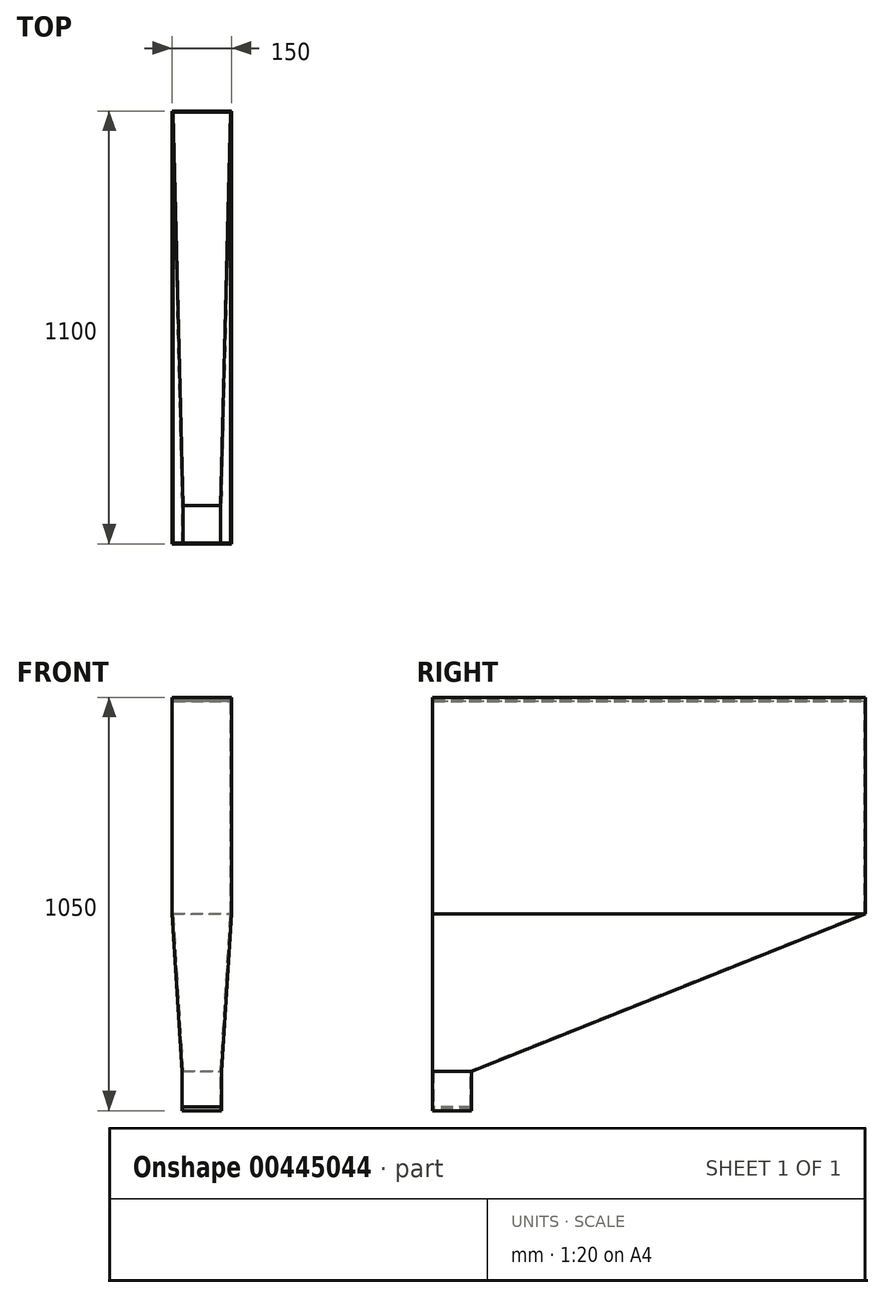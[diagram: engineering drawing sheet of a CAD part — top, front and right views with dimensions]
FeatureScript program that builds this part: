
annotation { "Feature Type Name" : "Feature", "Feature Type Description" : "" }
export const myFeature = defineFeature(function(context is Context, id is Id, definition is map)
    precondition{}
    {
        {
            var Q0;
            Q0=qCreatedBy(makeId("Front.planeOp"),FACE);
            var sketch = newSketch(context, id + "F0", { "sketchPlane" : qUnion([Q0])});
            skLineSegment(sketch, "E0.bottom", {"start": v(-75, 0) * mm, "end": v(75, 0) * mm});
            skLineSegment(sketch, "E0.top", {"start": v(-75, 550) * mm, "end": v(75, 550) * mm});
            skLineSegment(sketch, "E0.left", {"start": v(-75, 0) * mm, "end": v(-75, 550) * mm});
            skLineSegment(sketch, "E0.right", {"start": v(75, 0) * mm, "end": v(75, 550) * mm});
            skLineSegment(sketch, "E1.bottom", {"start": v(-50, -400) * mm, "end": v(50, -400) * mm});
            skLineSegment(sketch, "E1.top", {"start": v(-50, -500) * mm, "end": v(50, -500) * mm});
            skLineSegment(sketch, "E1.left", {"start": v(-50, -400) * mm, "end": v(-50, -500) * mm});
            skLineSegment(sketch, "E1.right", {"start": v(50, -400) * mm, "end": v(50, -500) * mm});
            skLineSegment(sketch, "E2", {"start": v(-75, 0) * mm, "end": v(-50, -400) * mm});
            skLineSegment(sketch, "E3", {"start": v(50, -400) * mm, "end": v(75, 0) * mm});
            skSolve(sketch);
        }
        {
            var Q0;
            Q0=makeQuery(id+"F0.imprint","IMPRINT",FACE,{"disambiguationData":[TD([[makeQuery(id+"F0.imprint","IMPRINT",EDGE,{"derivedFrom":sQuery(id+"F0.wireOp",EDGE,"E1.bottom")}),-1.0]])]});
            var Q1;
            Q1=makeQuery(id+"F0.imprint","IMPRINT",FACE,{"disambiguationData":[TD([[makeQuery(id+"F0.imprint","IMPRINT",EDGE,{"derivedFrom":sQuery(id+"F0.wireOp",EDGE,"E0.bottom")}),1.0]])]});
            var Q2;
            Q2=makeQuery(id+"F0.imprint","IMPRINT",FACE,{"disambiguationData":[TD([[makeQuery(id+"F0.imprint","IMPRINT",EDGE,{"derivedFrom":sQuery(id+"F0.wireOp",EDGE,"E0.bottom")}),-1.0]])]});
            extrude(context, id + "F1", {"entities" : qUnion([Q0, Q1, Q2]), "endBound" : BoundingType.SYMMETRIC, "depth" : 1100 * mm});
        }
        {
            var Q0;
            Q0=makeQuery(id+"F1.opExtrude","SWEPT_FACE",FACE,{"disambiguationData":[OSD([sQuery(id+"F0.wireOp",EDGE,"E0.right")])]});
            var sketch = newSketch(context, id + "F2", { "sketchPlane" : qUnion([Q0])});
            skLineSegment(sketch, "E4", {"start": v(550, 0) * mm, "end": v(550, -500) * mm});
            skLineSegment(sketch, "E5", {"start": v(550, -500) * mm, "end": v(-450, -500) * mm});
            skLineSegment(sketch, "E6", {"start": v(-450, -500) * mm, "end": v(-450, -400) * mm});
            skLineSegment(sketch, "E7", {"start": v(-450, -400) * mm, "end": v(550, 0) * mm});
            skSolve(sketch);
        }
        {
            var Q0;
            Q0=makeQuery(id+"F2.imprint","IMPRINT",FACE,{"disambiguationData":[TD([[makeQuery(id+"F2.imprint","IMPRINT",EDGE,{"derivedFrom":sQuery(id+"F2.wireOp",EDGE,"E4")}),-1.0]])]});
            extrude(context, id + "F3", {"entities" : qUnion([Q0]), "operationType" : NewBodyOperationType.REMOVE, "oppositeDirection" : true, "depth" : 150 * mm});
        }
        {
            var Q0;
            Q0=makeQuery(id+"F1.opExtrude","SWEPT_FACE",FACE,{"disambiguationData":[OSD([sQuery(id+"F0.wireOp",EDGE,"E0.top")])]});
            var Q1;
            Q1=makeQuery(id+"F1.opExtrude","SWEPT_FACE",FACE,{"disambiguationData":[OSD([sQuery(id+"F0.wireOp",EDGE,"E1.top")])]});
            shell(context, id + "F4", {"entities" : qUnion([Q0, Q1]), "thickness" : 2.5 * mm});
        }
        {
            var Q0;
            Q0=makeQuery(id+"F1.opExtrude","CAP_FACE",FACE,{"disambiguationData":[OSD([sQuery(id+"F0.wireOp",EDGE,"E0.top"),sQuery(id+"F0.wireOp",EDGE,"E0.left"),sQuery(id+"F0.wireOp",EDGE,"E0.right"),sQuery(id+"F0.wireOp",EDGE,"E1.top"),sQuery(id+"F0.wireOp",EDGE,"E1.left"),sQuery(id+"F0.wireOp",EDGE,"E1.right"),sQuery(id+"F0.wireOp",EDGE,"E2"),sQuery(id+"F0.wireOp",EDGE,"E3")])],"isStart":false});
            var sketch = newSketch(context, id + "F5", { "sketchPlane" : qUnion([Q0])});
            skLineSegment(sketch, "E8", {"start": v(-48.5, -500) * mm, "end": v(48.5, -500) * mm});
            skLineSegment(sketch, "E9", {"start": v(48.5, -500) * mm, "end": v(48.5, -495) * mm});
            skLineSegment(sketch, "E10", {"start": v(48.5, -495) * mm, "end": v(49.5, -495) * mm});
            skLineSegment(sketch, "E11", {"start": v(49.5, -495) * mm, "end": v(49.5, -490) * mm});
            skLineSegment(sketch, "E12", {"start": v(49.5, -490) * mm, "end": v(-49.5, -490) * mm});
            skLineSegment(sketch, "E13", {"start": v(-49.5, -490) * mm, "end": v(-49.5, -495) * mm});
            skLineSegment(sketch, "E14", {"start": v(-48.5, -500) * mm, "end": v(-48.5, -495) * mm});
            skLineSegment(sketch, "E15", {"start": v(-48.5, -495) * mm, "end": v(-49.5, -495) * mm});
            skSolve(sketch);
        }
        {
            var Q0;
            Q0=makeQuery(id+"F5.imprint","IMPRINT",FACE,{"disambiguationData":[TD([[makeQuery(id+"F5.imprint","IMPRINT",EDGE,{"derivedFrom":sQuery(id+"F5.wireOp",EDGE,"E8")}),1.0]])]});
            extrude(context, id + "F6", {"entities" : qUnion([Q0]), "operationType" : NewBodyOperationType.REMOVE, "oppositeDirection" : true, "depth" : 98.5 * mm});
        }
        {
            var Q0;
            Q0=makeQuery(id+"F1.opExtrude","CAP_FACE",FACE,{"disambiguationData":[OSD([sQuery(id+"F0.wireOp",EDGE,"E0.top"),sQuery(id+"F0.wireOp",EDGE,"E0.left"),sQuery(id+"F0.wireOp",EDGE,"E0.right"),sQuery(id+"F0.wireOp",EDGE,"E1.top"),sQuery(id+"F0.wireOp",EDGE,"E1.left"),sQuery(id+"F0.wireOp",EDGE,"E1.right"),sQuery(id+"F0.wireOp",EDGE,"E2"),sQuery(id+"F0.wireOp",EDGE,"E3")])],"isStart":true});
            var sketch = newSketch(context, id + "F7", { "sketchPlane" : qUnion([Q0])});
            skLineSegment(sketch, "E16", {"start": v(-74, 540) * mm, "end": v(74, 540) * mm});
            skLineSegment(sketch, "E17", {"start": v(74, 540) * mm, "end": v(74, 545) * mm});
            skLineSegment(sketch, "E18", {"start": v(72.5, 545) * mm, "end": v(74, 545) * mm});
            skLineSegment(sketch, "E19", {"start": v(72.5, 545) * mm, "end": v(72.5, 550) * mm});
            skLineSegment(sketch, "E20", {"start": v(72.5, 550) * mm, "end": v(-72.5, 550) * mm});
            skLineSegment(sketch, "E21", {"start": v(-72.5, 550) * mm, "end": v(-72.5, 545) * mm});
            skLineSegment(sketch, "E22", {"start": v(-74, 540) * mm, "end": v(-74, 545) * mm});
            skLineSegment(sketch, "E23", {"start": v(-72.5, 545) * mm, "end": v(-74, 545) * mm});
            skLineSegment(sketch, "E24", {"start": v(-72.5, 545) * mm, "end": v(72.5, 545) * mm});
            skSolve(sketch);
        }
        {
            var Q0;
            Q0=makeQuery(id+"F7.imprint","IMPRINT",FACE,{"disambiguationData":[TD([[makeQuery(id+"F7.imprint","IMPRINT",EDGE,{"derivedFrom":sQuery(id+"F7.wireOp",EDGE,"E19")}),1.0]])]});
            extrude(context, id + "F8", {"entities" : qUnion([Q0]), "operationType" : NewBodyOperationType.REMOVE, "oppositeDirection" : true, "depth" : 2.5 * mm});
        }
        {
            var Q0;
            Q0=makeQuery(id+"F7.imprint","IMPRINT",FACE,{"disambiguationData":[TD([[makeQuery(id+"F7.imprint","IMPRINT",EDGE,{"derivedFrom":sQuery(id+"F7.wireOp",EDGE,"E16")}),1.0]])]});
            extrude(context, id + "F9", {"entities" : qUnion([Q0]), "operationType" : NewBodyOperationType.REMOVE, "oppositeDirection" : true, "depth" : 1099 * mm});
        }
    });
